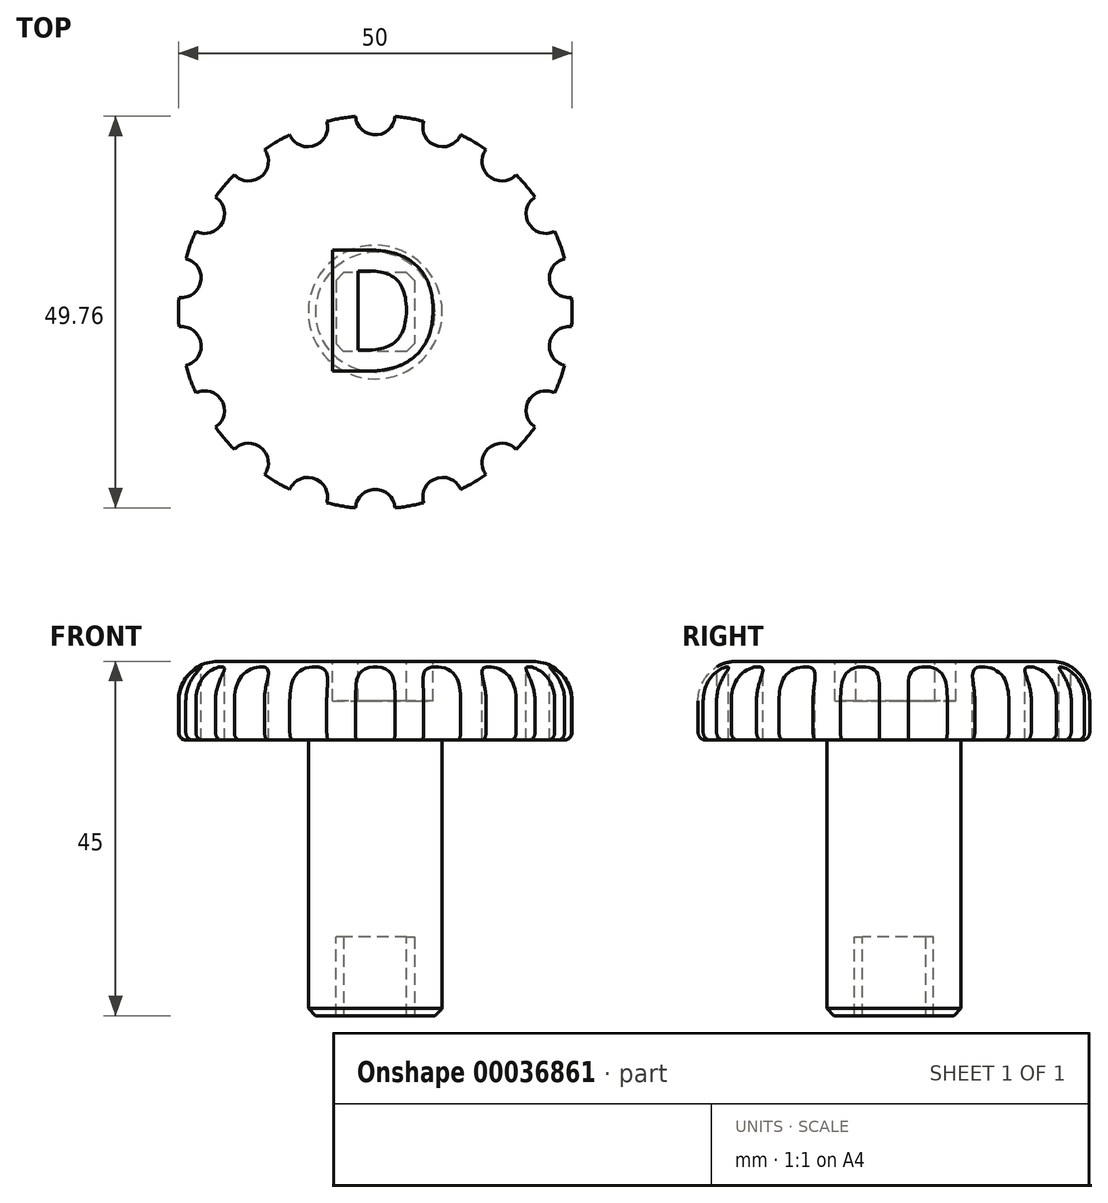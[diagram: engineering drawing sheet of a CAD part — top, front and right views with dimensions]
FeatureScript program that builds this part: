
annotation { "Feature Type Name" : "Feature", "Feature Type Description" : "" }
export const myFeature = defineFeature(function(context is Context, id is Id, definition is map)
    precondition{}
    {
        {
            var Q0;
            Q0=qCreatedBy(makeId("Top.planeOp"),FACE);
            var sketch = newSketch(context, id + "F0", { "sketchPlane" : qUnion([Q0])});
            skLineSegment(sketch, "E0.rect.bottom", {"start": v(5, 5) * mm, "end": v(-5, 5) * mm});
            skLineSegment(sketch, "E0.rect.top", {"start": v(5, -5) * mm, "end": v(-5, -5) * mm});
            skLineSegment(sketch, "E0.rect.left", {"start": v(5, 5) * mm, "end": v(5, -5) * mm});
            skLineSegment(sketch, "E0.rect.right", {"start": v(-5, 5) * mm, "end": v(-5, -5) * mm});
            skPoint(sketch, "E0.rect.middle", {"position": v(0, 0) * mm});
            skCircle(sketch, "E1", {"center": v(0, 0) * mm, "radius": 8.5 * mm});
            skSolve(sketch);
        }
        {
            var Q0;
            Q0=makeQuery(id+"F0.imprint","IMPRINT",FACE,{"disambiguationData":[TD([[makeQuery(id+"F0.imprint","IMPRINT",EDGE,{"derivedFrom":sQuery(id+"F0.wireOp",EDGE,"E0.rect.bottom")}),-1.0]])]});
            var Q1;
            Q1=makeQuery(id+"F0.imprint","IMPRINT",FACE,{"disambiguationData":[TD([[makeQuery(id+"F0.imprint","IMPRINT",EDGE,{"derivedFrom":sQuery(id+"F0.wireOp",EDGE,"E0.rect.bottom")}),1.0]])]});
            extrude(context, id + "F1", {"entities" : qUnion([Q0, Q1]), "depth" : 35 * mm});
        }
        {
            var Q0;
            Q0=makeQuery(id+"F0.imprint","IMPRINT",FACE,{"disambiguationData":[TD([[makeQuery(id+"F0.imprint","IMPRINT",EDGE,{"derivedFrom":sQuery(id+"F0.wireOp",EDGE,"E0.rect.bottom")}),1.0]])]});
            extrude(context, id + "F2", {"entities" : qUnion([Q0]), "operationType" : NewBodyOperationType.REMOVE, "depth" : 10 * mm});
        }
        {
            var Q0;
            Q0=makeQuery(id+"F2.boolean.opBoolean","COPY",EDGE,{"derivedFrom":makeQuery(id+"F2.opExtrude","SWEPT_EDGE",EDGE,{"disambiguationData":[OSD([sQuery(id+"F0.wireOp",EDGE,"E0.rect.top"),sQuery(id+"F0.wireOp",EDGE,"E0.rect.right")])]})});
            var Q1;
            Q1=makeQuery(id+"F2.boolean.opBoolean","COPY",EDGE,{"derivedFrom":makeQuery(id+"F2.opExtrude","SWEPT_EDGE",EDGE,{"disambiguationData":[OSD([sQuery(id+"F0.wireOp",EDGE,"E0.rect.bottom"),sQuery(id+"F0.wireOp",EDGE,"E0.rect.right")])]})});
            var Q2;
            Q2=makeQuery(id+"F2.boolean.opBoolean","COPY",EDGE,{"derivedFrom":makeQuery(id+"F2.opExtrude","SWEPT_EDGE",EDGE,{"disambiguationData":[OSD([sQuery(id+"F0.wireOp",EDGE,"E0.rect.bottom"),sQuery(id+"F0.wireOp",EDGE,"E0.rect.left")])]})});
            var Q3;
            Q3=makeQuery(id+"F2.boolean.opBoolean","COPY",EDGE,{"derivedFrom":makeQuery(id+"F2.opExtrude","SWEPT_EDGE",EDGE,{"disambiguationData":[OSD([sQuery(id+"F0.wireOp",EDGE,"E0.rect.top"),sQuery(id+"F0.wireOp",EDGE,"E0.rect.left")])]})});
            chamfer(context, id + "F3", {"entities" : qUnion([Q0, Q1, Q2, Q3]), "width" : 1 * mm, "tangentPropagation" : true});
        }
        {
            var Q0;
            Q0=makeQuery(id+"F1.opExtrude","CAP_FACE",FACE,{"disambiguationData":[OSD([sQuery(id+"F0.wireOp",EDGE,"E1")])],"isStart":false});
            var sketch = newSketch(context, id + "F4", { "sketchPlane" : qUnion([Q0])});
            skCircle(sketch, "E2", {"center": v(0, 0) * mm, "radius": 25 * mm});
            skSolve(sketch);
        }
        {
            var Q0;
            Q0 = qSketchRegion(id + "F4", true);
            var Q1;
            Q1=makeQuery(id+"F4.imprint","IMPRINT",FACE,{"disambiguationData":[TD([[makeQuery(id+"F4.imprint","IMPRINT",EDGE,{"derivedFrom":sQuery(id+"F4.wireOp",EDGE,"E2")}),1.0]])]});
            extrude(context, id + "F5", {"entities" : qUnion([Q0, Q1]), "operationType" : NewBodyOperationType.ADD, "depth" : 10 * mm});
        }
        {
            var Q0;
            Q0=makeQuery(id+"F1.opExtrude","CAP_EDGE",EDGE,{"disambiguationData":[OSD([sQuery(id+"F0.wireOp",EDGE,"E1")])],"isStart":false});
            var Q1;
            Q1=makeQuery(id+"F5.opExtrude","CAP_EDGE",EDGE,{"disambiguationData":[OSD([sQuery(id+"F4.wireOp",EDGE,"E2")])],"isStart":false});
            fillet(context, id + "F6", {"entities" : qUnion([Q0, Q1]), "radius" : 5 * mm, "tangentPropagation" : true, "allowEdgeOverflow" : false});
        }
        {
            var Q0;
            Q0=makeQuery(id+"F5.opExtrude","CAP_FACE",FACE,{"disambiguationData":[OSD([sQuery(id+"F4.wireOp",EDGE,"E2")])],"isStart":false});
            var sketch = newSketch(context, id + "F7", { "sketchPlane" : qUnion([Q0])});
            skText(sketch, "E3", { "text": "D", "fontName": "OpenSans-Bold.ttf"});
            const initialGuessF7  = {"E3": [-0.00735, -0.0075, 1, 0, 0.0155]};
            skSetInitialGuess(sketch, initialGuessF7);
            skSolve(sketch);
        }
        {
            var Q0;
            {var subQ0=sQuery(id+"F4.wireOp",EDGE,"E2");Q0=makeQuery(id+"F11.boolean.opBoolean","SPLIT",EDGE,{"disambiguationData":[TD([makeQuery(id+"F5.opExtrude","SWEPT_FACE",FACE,{"disambiguationData":[OSD([subQ0])]}),makeQuery(id+"F5.opExtrude","CAP_FACE",FACE,{"disambiguationData":[OSD([subQ0])],"isStart":true}),makeQuery(id+"F11.opExtrude","SWEPT_FACE",FACE,{"disambiguationData":[OSD([sQuery(id+"F10.wireOp",EDGE,"E4")])]}),makeQuery(id+"F11.opExtrude","SWEPT_FACE",FACE,{"disambiguationData":[OSD([sQuery(id+"F10.wireOp",EDGE,"E6.1.17.0")])]})])],"derivedFrom":makeQuery(id+"F5.opExtrude","CAP_EDGE",EDGE,{"disambiguationData":[OSD([subQ0])],"isStart":true})});}
            fillet(context, id + "F8", {"entities" : qUnion([Q0]), "radius" : 1 * mm, "tangentPropagation" : true, "allowEdgeOverflow" : false});
        }
        {
            var Q0;
            Q0=makeQuery(id+"F7.imprint","IMPRINT",FACE,{"disambiguationData":[TD([[makeQuery(id+"F7.imprint","IMPRINT",EDGE,{"derivedFrom":sQuery(id+"F7.wireOp",EDGE,"E3.sketch_text.stroke-0")}),-1.0]])]});
            var Q1;
            Q1 = qSketchRegion(id + "F7", true);
            extrude(context, id + "F9", {"entities" : qUnion([Q0, Q1]), "operationType" : NewBodyOperationType.REMOVE, "oppositeDirection" : true, "depth" : 5 * mm});
        }
        {
            var Q0;
            Q0=makeQuery(id+"F5.opExtrude","CAP_FACE",FACE,{"disambiguationData":[OSD([sQuery(id+"F4.wireOp",EDGE,"E2")])],"isStart":false});
            var sketch = newSketch(context, id + "F10", { "sketchPlane" : qUnion([Q0])});
            skCircle(sketch, "E4", {"center": v(0, -25) * mm, "radius": 2.5 * mm});
            skCircle(sketch, "E5.1.0", {"center": v(8.55, -23.5) * mm, "radius": 2.5 * mm});
            skCircle(sketch, "E5.2.0", {"center": v(16.07, -19.15) * mm, "radius": 2.5 * mm});
            skCircle(sketch, "E5.3.0", {"center": v(21.65, -12.5) * mm, "radius": 2.5 * mm});
            skCircle(sketch, "E5.4.0", {"center": v(24.62, -4.34) * mm, "radius": 2.5 * mm});
            skCircle(sketch, "E5.5.0", {"center": v(24.62, 4.34) * mm, "radius": 2.5 * mm});
            skCircle(sketch, "E5.6.0", {"center": v(21.65, 12.5) * mm, "radius": 2.5 * mm});
            skCircle(sketch, "E5.7.0", {"center": v(16.07, 19.15) * mm, "radius": 2.5 * mm});
            skCircle(sketch, "E5.8.0", {"center": v(8.55, 23.5) * mm, "radius": 2.5 * mm});
            skCircle(sketch, "E5.9.0", {"center": v(0, 25) * mm, "radius": 2.5 * mm});
            skCircle(sketch, "E5.10.0", {"center": v(-8.55, 23.5) * mm, "radius": 2.5 * mm});
            skCircle(sketch, "E5.11.0", {"center": v(-16.07, 19.15) * mm, "radius": 2.5 * mm});
            skCircle(sketch, "E5.12.0", {"center": v(-21.65, 12.5) * mm, "radius": 2.5 * mm});
            skCircle(sketch, "E5.13.0", {"center": v(-24.62, 4.34) * mm, "radius": 2.5 * mm});
            skCircle(sketch, "E5.14.0", {"center": v(-24.62, -4.34) * mm, "radius": 2.5 * mm});
            skPoint(sketch, "E5.center", {"position": v(0, 0) * mm});
            skCircle(sketch, "E6.1.15.0", {"center": v(-21.65, -12.5) * mm, "radius": 2.5 * mm});
            skCircle(sketch, "E6.1.16.0", {"center": v(-16.07, -19.15) * mm, "radius": 2.5 * mm});
            skCircle(sketch, "E6.1.17.0", {"center": v(-8.55, -23.5) * mm, "radius": 2.5 * mm});
            skCircle(sketch, "E7", {"center": v(0, 0) * mm, "radius": 25 * mm, "construction": true});
            skSolve(sketch);
        }
        {
            var Q0;
            Q0 = qSketchRegion(id + "F10", true);
            extrude(context, id + "F11", {"entities" : qUnion([Q0]), "operationType" : NewBodyOperationType.REMOVE, "oppositeDirection" : true, "depth" : 25 * mm});
        }
        {
            var Q0;
            Q0=makeQuery(id+"F1.opExtrude","CAP_EDGE",EDGE,{"disambiguationData":[OSD([sQuery(id+"F0.wireOp",EDGE,"E1")])],"isStart":true});
            chamfer(context, id + "F12", {"entities" : qUnion([Q0]), "width" : .9 * mm, "tangentPropagation" : true});
        }
    });
